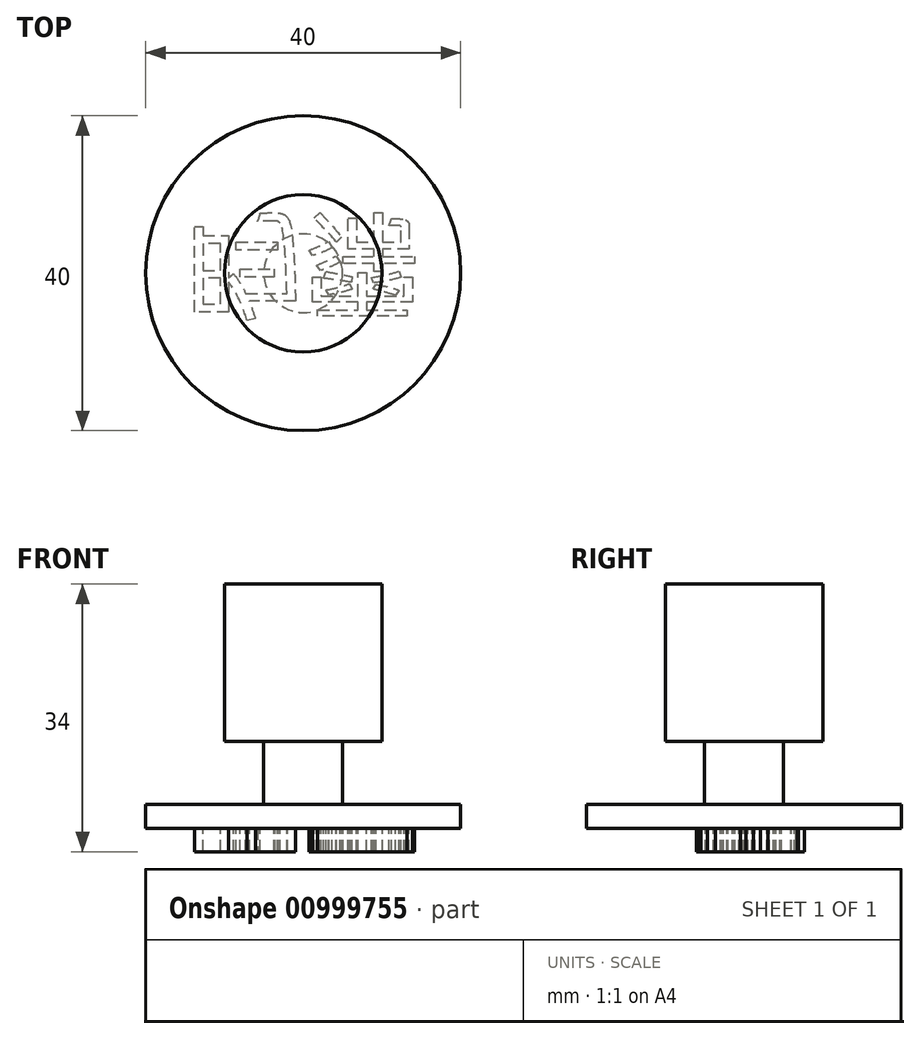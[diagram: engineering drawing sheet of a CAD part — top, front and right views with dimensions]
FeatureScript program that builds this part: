
annotation { "Feature Type Name" : "Feature", "Feature Type Description" : "" }
export const myFeature = defineFeature(function(context is Context, id is Id, definition is map)
    precondition{}
    {
        {
            var Q0;
            Q0=qCreatedBy(makeId("Top.planeOp"),FACE);
            var sketch = newSketch(context, id + "F0", { "sketchPlane" : qUnion([Q0])});
            skCircle(sketch, "E0", {"center": v(0, 0) * mm, "radius": 20 * mm});
            skSolve(sketch);
        }
        {
            var Q0;
            Q0 = qSketchRegion(id + "F0", true);
            extrude(context, id + "F1", {"entities" : qUnion([Q0]), "depth" : 3 * mm, "offsetDistance" : 25 * mm});
        }
        {
            var Q0;
            Q0=makeQuery(id+"F1.opExtrude","CAP_FACE",FACE,{"disambiguationData":[OSD([sQuery(id+"F0.wireOp",EDGE,"E0")])],"isStart":false});
            var sketch = newSketch(context, id + "F2", { "sketchPlane" : qUnion([Q0])});
            skCircle(sketch, "E1", {"center": v(0, 0) * mm, "radius": 5 * mm});
            skSolve(sketch);
        }
        {
            var Q0;
            Q0 = qSketchRegion(id + "F2", true);
            var Q1;
            Q1=sQuery(id+"F2.wireOp",EDGE,"E1");
            extrude(context, id + "F3", {"entities" : qUnion([Q0]), "operationType" : NewBodyOperationType.ADD, "surfaceEntities" : qUnion([Q1]), "depth" : 8 * mm, "offsetDistance" : 25 * mm});
        }
        {
            var Q0;
            Q0=makeQuery(id+"F3.opExtrude","CAP_FACE",FACE,{"disambiguationData":[OSD([sQuery(id+"F2.wireOp",EDGE,"E1")])],"isStart":false});
            var sketch = newSketch(context, id + "F4", { "sketchPlane" : qUnion([Q0])});
            skCircle(sketch, "E2", {"center": v(0, 0) * mm, "radius": 10 * mm});
            skSolve(sketch);
        }
        {
            var Q0;
            Q0 = qSketchRegion(id + "F4", true);
            extrude(context, id + "F5", {"entities" : qUnion([Q0]), "depth" : 20 * mm, "offsetDistance" : 25 * mm});
        }
        {
            var Q0;
            Q0=makeQuery(id+"F1.opExtrude","CAP_FACE",FACE,{"disambiguationData":[OSD([sQuery(id+"F0.wireOp",EDGE,"E0")])],"isStart":true});
            var sketch = newSketch(context, id + "F6", { "sketchPlane" : qUnion([Q0])});
            skText(sketch, "E3", { "text": "昀霈", "fontName": "NotoSansCJKtc-Regular.otf"});
            const initialGuessF6  = {"E3": [-0.015, -0.00654, 1, 0, 0.01082]};
            skSetInitialGuess(sketch, initialGuessF6);
            skSolve(sketch);
        }
        {
            var Q0;
            Q0 = qSketchRegion(id + "F6", true);
            extrude(context, id + "F7", {"entities" : qUnion([Q0]), "operationType" : NewBodyOperationType.ADD, "depth" : 3 * mm, "offsetDistance" : 25 * mm});
        }
    });
